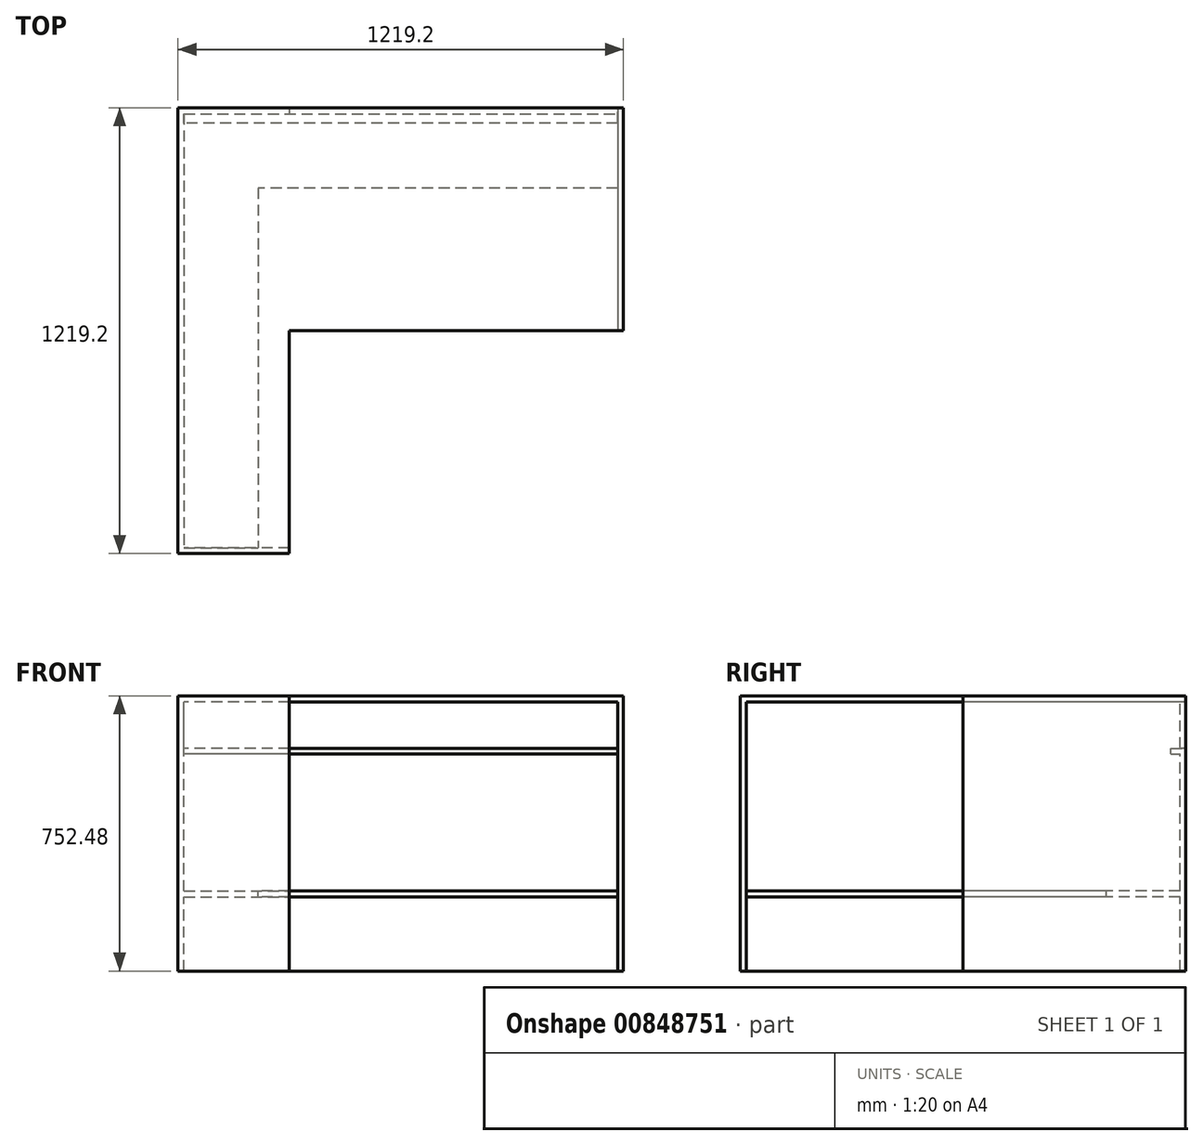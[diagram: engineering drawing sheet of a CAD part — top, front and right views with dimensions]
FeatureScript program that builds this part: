
annotation { "Feature Type Name" : "Feature", "Feature Type Description" : "" }
export const myFeature = defineFeature(function(context is Context, id is Id, definition is map)
    precondition{}
    {
        {
            var Q0;
            Q0=qCreatedBy(makeId("Top.planeOp"),FACE);
            var sketch = newSketch(context, id + "F0", { "sketchPlane" : qUnion([Q0])});
            skLineSegment(sketch, "E0.bottom", {"start": v(-609.6, 304.8) * mm, "end": v(609.6, 304.8) * mm});
            skLineSegment(sketch, "E0.top", {"start": v(-609.6, -304.8) * mm, "end": v(609.6, -304.8) * mm});
            skLineSegment(sketch, "E0.left", {"start": v(-609.6, 304.8) * mm, "end": v(-609.6, -304.8) * mm});
            skLineSegment(sketch, "E0.right", {"start": v(609.6, 304.8) * mm, "end": v(609.6, -304.8) * mm});
            skSolve(sketch);
        }
        {
            var Q0;
            Q0 = qSketchRegion(id + "F0", true);
            extrude(context, id + "F1", {"entities" : qUnion([Q0]), "depth" : 15.88 * mm, "offsetDistance" : 25.4 * mm});
        }
        {
            var Q0;
            Q0=makeQuery(id+"F1.opExtrude","CAP_FACE",FACE,{"disambiguationData":[OSD([sQuery(id+"F0.wireOp",EDGE,"E0.bottom"),sQuery(id+"F0.wireOp",EDGE,"E0.top"),sQuery(id+"F0.wireOp",EDGE,"E0.left"),sQuery(id+"F0.wireOp",EDGE,"E0.right")])],"isStart":true});
            var sketch = newSketch(context, id + "F2", { "sketchPlane" : qUnion([Q0])});
            skLineSegment(sketch, "E1.0", {"start": v(-593.72, -288.93) * mm, "end": v(-593.73, 304.8) * mm});
            skLineSegment(sketch, "E1.1", {"start": v(-593.72, -288.93) * mm, "end": v(593.73, -288.92) * mm});
            skLineSegment(sketch, "E1.2", {"start": v(593.73, -288.93) * mm, "end": v(593.73, 304.8) * mm});
            skLineSegment(sketch, "E2.0", {"start": v(-609.6, -304.8) * mm, "end": v(-609.6, 304.8) * mm});
            skLineSegment(sketch, "E2.1", {"start": v(-609.6, -304.8) * mm, "end": v(609.6, -304.8) * mm});
            skLineSegment(sketch, "E2.2", {"start": v(609.6, -304.8) * mm, "end": v(609.6, 304.8) * mm});
            skLineSegment(sketch, "E3", {"start": v(-609.6, 304.8) * mm, "end": v(-593.73, 304.8) * mm});
            skLineSegment(sketch, "E4", {"start": v(609.6, 304.8) * mm, "end": v(593.73, 304.8) * mm});
            skSolve(sketch);
        }
        {
            var Q0;
            Q0 = qSketchRegion(id + "F2", true);
            extrude(context, id + "F3", {"entities" : qUnion([Q0]), "operationType" : NewBodyOperationType.ADD, "depth" : 736.6 * mm, "offsetDistance" : 25.4 * mm});
        }
        {
            var Q0;
            Q0=makeQuery(id+"Fn36FfQxMxu1gRP_1.boolean.opBoolean","SPLIT",FACE,{"disambiguationData":[TD([makeQuery(id+"Fn36FfQxMxu1gRP_1.opExtrude","SWEPT_FACE",FACE,{"disambiguationData":[OSD([sQuery(id+"F4kHf1HfsFYkJkB_1.wireOp",EDGE,"5O5Rj8YB-KiGO-cAIv-NlwB-YvEprwQRDa3C")])]})])],"derivedFrom":makeQuery(id+"F3.opExtrude","SWEPT_FACE",FACE,{"disambiguationData":[OSD([sQuery(id+"F2.wireOp",EDGE,"E1.1")])]})});
            var sketch = newSketch(context, id + "F4", { "sketchPlane" : qUnion([Q0])});
            skLineSegment(sketch, "E5", {"start": v(593.73, -127) * mm, "end": v(-593.72, -127) * mm});
            skLineSegment(sketch, "E6", {"start": v(593.73, -127) * mm, "end": v(593.73, -142.87) * mm});
            skLineSegment(sketch, "E7", {"start": v(593.73, -142.87) * mm, "end": v(-593.72, -142.88) * mm});
            skLineSegment(sketch, "E8", {"start": v(-593.72, -142.88) * mm, "end": v(-593.72, -127) * mm});
            skSolve(sketch);
        }
        {
            var Q0;
            Q0 = qSketchRegion(id + "F4", true);
            extrude(context, id + "F5", {"entities" : qUnion([Q0]), "operationType" : NewBodyOperationType.ADD, "depth" : 25.4 * mm, "offsetDistance" : 25.4 * mm});
        }
        {
            var Q0;
            Q0=makeQuery(id+"F5.boolean.opBoolean","SPLIT",FACE,{"disambiguationData":[TD([makeQuery(id+"F5.opExtrude","SWEPT_FACE",FACE,{"disambiguationData":[OSD([sQuery(id+"F4.wireOp",EDGE,"E5")])]})])],"derivedFrom":makeQuery(id+"Fn36FfQxMxu1gRP_1.boolean.opBoolean","SPLIT",FACE,{"disambiguationData":[TD([makeQuery(id+"Fn36FfQxMxu1gRP_1.opExtrude","SWEPT_FACE",FACE,{"disambiguationData":[OSD([sQuery(id+"F4kHf1HfsFYkJkB_1.wireOp",EDGE,"5O5Rj8YB-KiGO-cAIv-NlwB-YvEprwQRDa3C")])]})])],"derivedFrom":makeQuery(id+"F3.opExtrude","SWEPT_FACE",FACE,{"disambiguationData":[OSD([sQuery(id+"F2.wireOp",EDGE,"E1.1")])]})})});
            var sketch = newSketch(context, id + "F6", { "sketchPlane" : qUnion([Q0])});
            skLineSegment(sketch, "E9.bottom", {"start": v(593.73, 0) * mm, "end": v(-304.8, 0) * mm});
            skLineSegment(sketch, "E9.top", {"start": v(593.73, -127) * mm, "end": v(-304.8, -127) * mm});
            skLineSegment(sketch, "E9.left", {"start": v(593.73, 0) * mm, "end": v(593.73, -127) * mm});
            skLineSegment(sketch, "E9.right", {"start": v(-304.8, 0) * mm, "end": v(-304.8, -127) * mm});
            skSolve(sketch);
        }
        {
            var Q0;
            Q0 = qSketchRegion(id + "F6", true);
            extrude(context, id + "F7", {"entities" : qUnion([Q0]), "operationType" : NewBodyOperationType.REMOVE, "oppositeDirection" : true, "depth" : 25.4 * mm, "offsetDistance" : 25.4 * mm});
        }
        {
            var Q0;
            Q0=makeQuery(id+"F3.boolean.opBoolean","MERGE",FACE,{"derivedFrom":[makeQuery(id+"F1.opExtrude","SWEPT_FACE",FACE,{"disambiguationData":[OSD([sQuery(id+"F0.wireOp",EDGE,"E0.top")])]}),makeQuery(id+"F3.opExtrude","SWEPT_FACE",FACE,{"disambiguationData":[OSD([sQuery(id+"F2.wireOp",EDGE,"E3")])]}),makeQuery(id+"F3.opExtrude","SWEPT_FACE",FACE,{"disambiguationData":[OSD([sQuery(id+"F2.wireOp",EDGE,"E4")])]})]});
            var sketch = newSketch(context, id + "F8", { "sketchPlane" : qUnion([Q0])});
            skLineSegment(sketch, "E10", {"start": v(-304.8, 15.88) * mm, "end": v(-304.8, 0) * mm});
            skLineSegment(sketch, "E11", {"start": v(-304.8, 15.88) * mm, "end": v(-609.6, 15.88) * mm});
            skLineSegment(sketch, "E12", {"start": v(-609.6, 15.87) * mm, "end": v(-609.6, -736.6) * mm});
            skLineSegment(sketch, "E13", {"start": v(-609.6, -736.6) * mm, "end": v(-593.73, -736.6) * mm});
            skLineSegment(sketch, "E14", {"start": v(-593.73, -736.6) * mm, "end": v(-593.73, 0) * mm});
            skLineSegment(sketch, "E15", {"start": v(-593.73, 0) * mm, "end": v(-304.8, 0) * mm});
            skSolve(sketch);
        }
        {
            var Q0;
            Q0 = qSketchRegion(id + "F8", true);
            extrude(context, id + "F9", {"entities" : qUnion([Q0]), "operationType" : NewBodyOperationType.ADD, "depth" : 609.6 * mm, "offsetDistance" : 25.4 * mm});
        }
        {
            var Q0;
            Q0=makeQuery(id+"F9.boolean.opBoolean","MERGE",FACE,{"derivedFrom":[makeQuery(id+"F3.opExtrude","SWEPT_FACE",FACE,{"disambiguationData":[OSD([sQuery(id+"F2.wireOp",EDGE,"E1.0")])]}),makeQuery(id+"F9.opExtrude","SWEPT_FACE",FACE,{"disambiguationData":[OSD([sQuery(id+"F8.wireOp",EDGE,"E14")])]})]});
            var sketch = newSketch(context, id + "F10", { "sketchPlane" : qUnion([Q0])});
            skLineSegment(sketch, "E16.bottom", {"start": v(-914.4, -736.6) * mm, "end": v(-898.53, -736.6) * mm});
            skLineSegment(sketch, "E16.top", {"start": v(-914.4, 0) * mm, "end": v(-898.53, 0) * mm});
            skLineSegment(sketch, "E16.left", {"start": v(-914.4, -736.6) * mm, "end": v(-914.4, 0) * mm});
            skLineSegment(sketch, "E16.right", {"start": v(-898.53, -736.6) * mm, "end": v(-898.53, 0) * mm});
            skSolve(sketch);
        }
        {
            var Q0;
            Q0 = qSketchRegion(id + "F10", true);
            extrude(context, id + "F11", {"entities" : qUnion([Q0]), "operationType" : NewBodyOperationType.ADD, "depth" : 288.93 * mm, "offsetDistance" : 25.4 * mm});
        }
        {
            var Q0;
            Q0=makeQuery(id+"F11.opExtrude","SWEPT_FACE",FACE,{"disambiguationData":[OSD([sQuery(id+"F10.wireOp",EDGE,"E16.right")])]});
            var sketch = newSketch(context, id + "F12", { "sketchPlane" : qUnion([Q0])});
            skLineSegment(sketch, "E17.top", {"start": v(593.72, -533.4) * mm, "end": v(390.52, -533.4) * mm});
            skLineSegment(sketch, "E18", {"start": v(593.72, -533.4) * mm, "end": v(593.72, -517.52) * mm});
            skLineSegment(sketch, "E19", {"start": v(593.72, -517.52) * mm, "end": v(390.52, -517.52) * mm});
            skLineSegment(sketch, "E20", {"start": v(390.52, -533.4) * mm, "end": v(390.52, -517.52) * mm});
            skSolve(sketch);
        }
        {
            var Q0;
            Q0 = qSketchRegion(id + "F12", true);
            extrude(context, id + "F13", {"entities" : qUnion([Q0]), "operationType" : NewBodyOperationType.ADD, "depth" : 1187.45 * mm, "offsetDistance" : 25.4 * mm});
        }
        {
            var Q0;
            Q0=makeQuery(id+"F13.opExtrude","SWEPT_FACE",FACE,{"disambiguationData":[OSD([sQuery(id+"F12.wireOp",EDGE,"E20")])]});
            var sketch = newSketch(context, id + "F14", { "sketchPlane" : qUnion([Q0])});
            skLineSegment(sketch, "E21.bottom", {"start": v(288.92, -517.52) * mm, "end": v(85.72, -517.52) * mm});
            skLineSegment(sketch, "E21.top", {"start": v(288.92, -533.4) * mm, "end": v(85.72, -533.4) * mm});
            skLineSegment(sketch, "E21.left", {"start": v(288.92, -517.52) * mm, "end": v(288.92, -533.4) * mm});
            skLineSegment(sketch, "E21.right", {"start": v(85.72, -517.52) * mm, "end": v(85.72, -533.4) * mm});
            skSolve(sketch);
        }
        {
            var Q0;
            Q0 = qSketchRegion(id + "F14", true);
            extrude(context, id + "F15", {"entities" : qUnion([Q0]), "operationType" : NewBodyOperationType.ADD, "depth" : 984.25 * mm, "offsetDistance" : 25.4 * mm});
        }
    });
